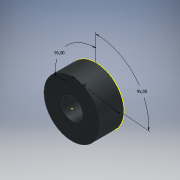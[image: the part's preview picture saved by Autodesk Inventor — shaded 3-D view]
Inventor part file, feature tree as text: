
AUTODESK INVENTOR PART (.ipt)
format: ipt  version: 2018 (Build 220112000, 112)  size: 118,272 bytes
history: native  units: mm
features: sketch x3, extrude x1
ambient origin geometry x8: Origin, YZ Plane, XZ Plane, XY Plane, X Axis, Y Axis, Z Axis, Center Point
bodies: Solido1 (feature_tree)
feature tree (4):
  extrude  "Estrusione1"  Depth=30.0mm
  sketch  "Schizzo2"
  sketch  "Schizzo3"
  sketch  "Schizzo1"
